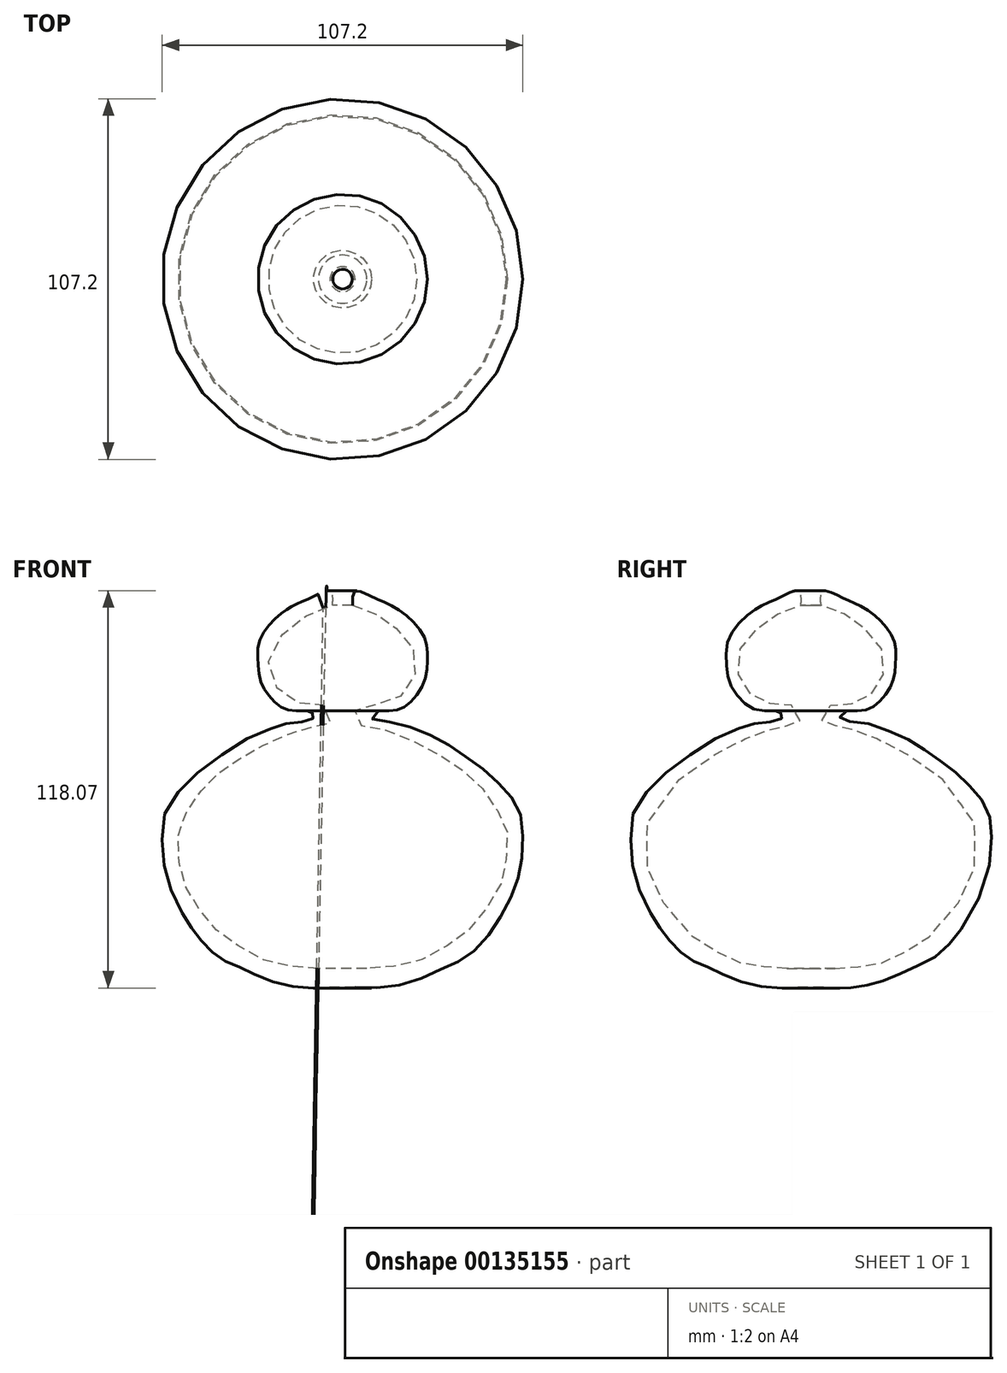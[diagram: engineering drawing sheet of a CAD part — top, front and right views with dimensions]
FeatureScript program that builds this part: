
annotation { "Feature Type Name" : "Feature", "Feature Type Description" : "" }
export const myFeature = defineFeature(function(context is Context, id is Id, definition is map)
    precondition{}
    {
        {
            var Q0;
            Q0=qCreatedBy(makeId("Front.planeOp"),FACE);
            var sketch = newSketch(context, id + "F0", { "sketchPlane" : qUnion([Q0])});
            skLineSegment(sketch, "E0", {"start": v(0, 73.36) * mm, "end": v(0, -73.1) * mm});
            skFitSpline(sketch, "E1", {"points": [v(-2.96, 64.96) * mm, v(-9.14, 62.74) * mm, v(-14.08, 59.53) * mm, v(-19.02, 55.08) * mm, v(-21.98, 48.66) * mm, v(-20.5, 42) * mm, v(-16.05, 37.05) * mm, v(-10.62, 35.57) * mm, v(-4.2, 34.33) * mm, v(-3.46, 30.14) * mm, v(-6.92, 29.15) * mm, v(-13.34, 27.67) * mm, v(-21.24, 24.46) * mm, v(-29.14, 20.26) * mm, v(-35.81, 15.81) * mm, v(-41.25, 10.87) * mm, v(-45.2, 4.94) * mm, v(-48.65, 0) * mm, v(-48.65, -7.16) * mm, v(-48.4, -13.83) * mm, v(-45.94, -20) * mm, v(-41.5, -26.92) * mm, v(-36.06, -32.84) * mm, v(-30.13, -36.8) * mm, v(-22.72, -40.75) * mm, v(-14.32, -42.48) * mm, v(-7.16, -42.97) * mm], "startDerivative": vector(-171.28, -51.8) * mm, "endDerivative": vector(177.7, -9.13) * mm});
            skLineSegment(sketch, "E2", {"start": v(-7.16, -42.97) * mm, "end": v(0, -42.97) * mm});
            skLineSegment(sketch, "E3", {"start": v(0, -42.97) * mm, "end": v(0, -48.65) * mm});
            skLineSegment(sketch, "E4", {"start": v(0, -48.65) * mm, "end": v(-3.7, -48.65) * mm});
            skFitSpline(sketch, "E5", {"points": [v(-3.7, -48.65) * mm, v(-12.35, -48.65) * mm, v(-22.23, -46.43) * mm, v(-29.88, -42.97) * mm, v(-35.81, -40.25) * mm, v(-41.5, -35.31) * mm, v(-46.68, -28.15) * mm, v(-50.63, -20.5) * mm, v(-52.85, -13.33) * mm, v(-53.6, -4.69) * mm, v(-52.6, 3.7) * mm, v(-48.9, 9.39) * mm, v(-43.47, 14.82) * mm, v(-36.8, 19.76) * mm, v(-30.38, 24.2) * mm, v(-22.97, 27.67) * mm, v(-14.57, 30.14) * mm, v(-8.9, 31.12) * mm, v(-9.14, 33.1) * mm, v(-14.82, 33.6) * mm, v(-19.76, 35.82) * mm, v(-24.2, 42) * mm, v(-25.2, 48.9) * mm, v(-24.7, 54.34) * mm, v(-20.5, 60.51) * mm, v(-14.32, 64.96) * mm, v(-9.39, 67.18) * mm, v(-3.7, 69.16) * mm, v(-2.96, 64.96) * mm], "startDerivative": vector(-213.17, -10.34) * mm, "endDerivative": vector(-10.47, -202.96) * mm});
            skSolve(sketch);
        }
        {
            var Q0;
            Q0=makeQuery(id+"F0.imprint","IMPRINT",FACE,{"disambiguationData":[TD([[makeQuery(id+"F0.imprint","IMPRINT",EDGE,{"derivedFrom":sQuery(id+"F0.wireOp",EDGE,"E1")}),-1.0]])]});
            var Q1;
            Q1=sQuery(id+"F0.wireOp",EDGE,"E0");
            revolve(context, id + "F1", {"entities" : qUnion([Q0]), "axis" : qUnion([Q1]), "revolveType" : RevolveType.FULL});
        }
    });
